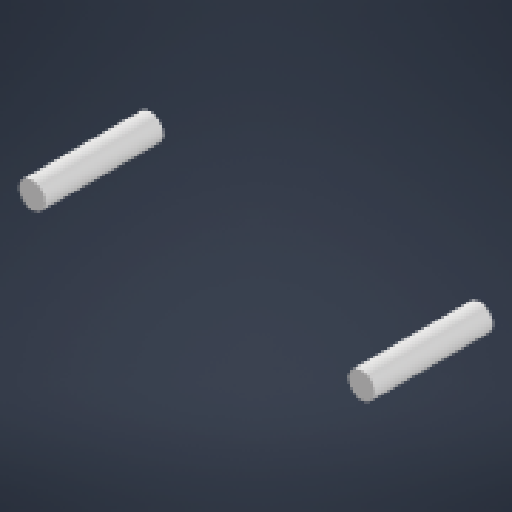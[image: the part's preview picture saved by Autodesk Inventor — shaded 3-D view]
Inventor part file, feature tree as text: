
AUTODESK INVENTOR PART (.ipt)
format: ipt  version: 2024 (Build 280153000, 153)  size: 128,512 bytes
history: native  units: mm
features: other x1, extrude x1, sketch x1
ambient origin geometry x8: Origin, YZ Plane, XZ Plane, XY Plane, X Axis, Y Axis, Z Axis, Center Point
bodies: Body1 (feature_tree)
feature tree (3):
  other  "Sólido1"
  extrude  "Extrusión1"  Depth=18.0mm
  sketch  "Boceto1"  dims[d0=4.0mm d1=4.0mm d2=50.0mm d3=124.2mm d4=18.0mm d5=0.0mm]
